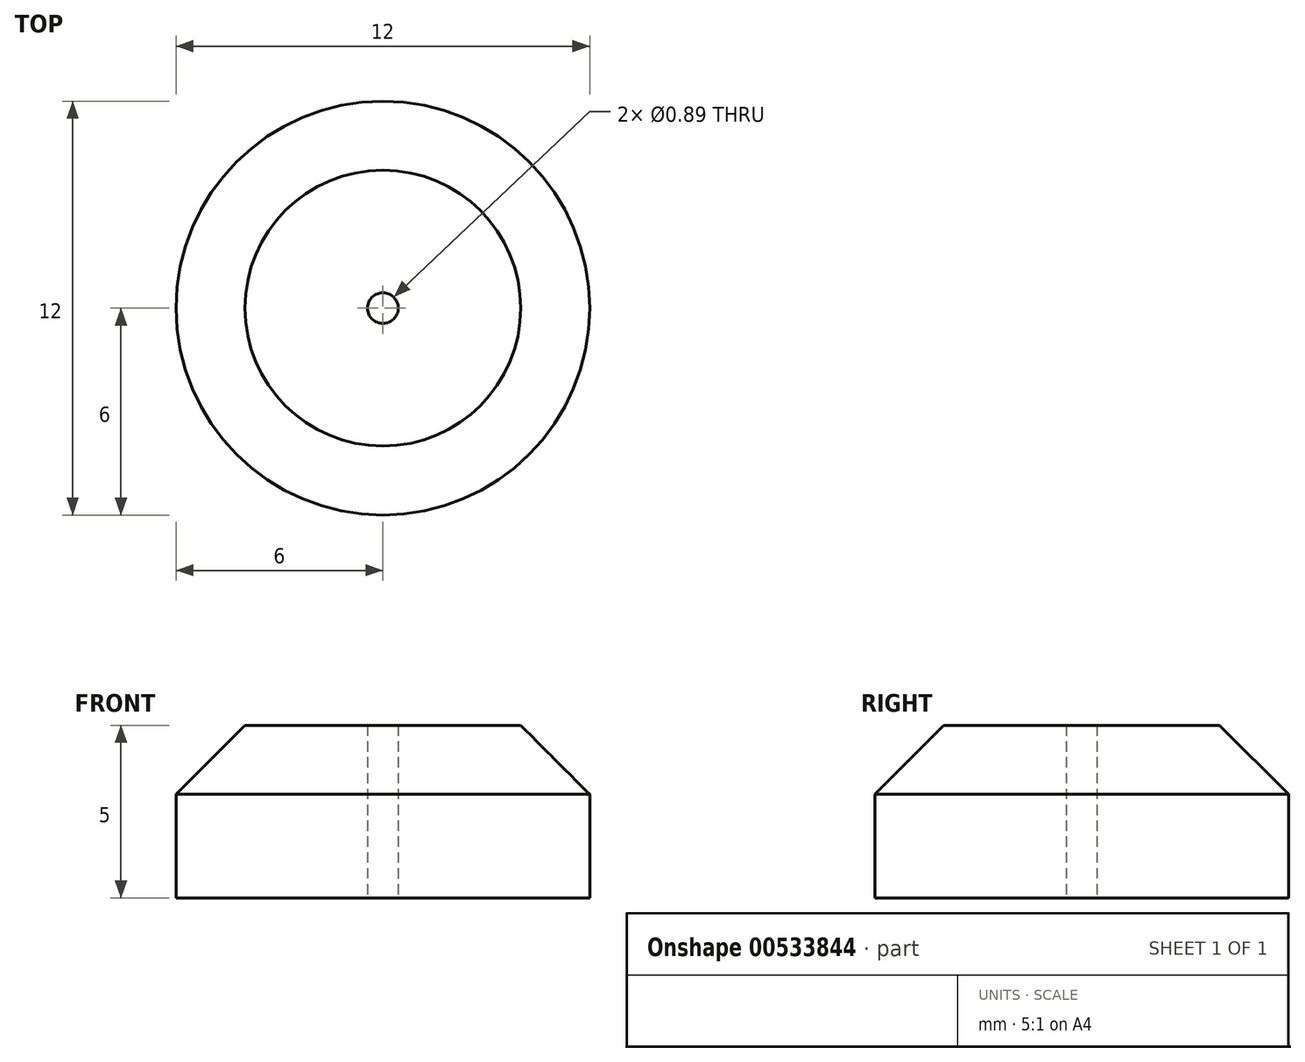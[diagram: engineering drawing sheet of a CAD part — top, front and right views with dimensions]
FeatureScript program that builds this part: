
annotation { "Feature Type Name" : "Feature", "Feature Type Description" : "" }
export const myFeature = defineFeature(function(context is Context, id is Id, definition is map)
    precondition{}
    {
        {
            var Q0;
            Q0=qCreatedBy(makeId("Top.planeOp"),FACE);
            var sketch = newSketch(context, id + "F0", { "sketchPlane" : qUnion([Q0])});
            skCircle(sketch, "E0", {"center": v(0, 0) * mm, "radius": 6 * mm});
            skCircle(sketch, "E1", {"center": v(0, 0) * mm, "radius": 0.45 * mm});
            skCircle(sketch, "E2", {"center": v(0, 0) * mm, "radius": 5 * mm});
            skSolve(sketch);
        }
        {
            var Q0;
            Q0=makeQuery(id+"F0.imprint","IMPRINT",FACE,{"disambiguationData":[TD([[makeQuery(id+"F0.imprint","IMPRINT",EDGE,{"derivedFrom":sQuery(id+"F0.wireOp",EDGE,"E1")}),-1.0]])]});
            var Q1;
            Q1=makeQuery(id+"F0.imprint","IMPRINT",FACE,{"disambiguationData":[TD([[makeQuery(id+"F0.imprint","IMPRINT",EDGE,{"derivedFrom":sQuery(id+"F0.wireOp",EDGE,"E0")}),1.0]])]});
            extrude(context, id + "F1", {"entities" : qUnion([Q0, Q1]), "depth" : 5 * mm, "offsetDistance" : 25.4 * mm});
        }
        {
            var Q0;
            Q0=makeQuery(id+"F1.opExtrude","CAP_EDGE",EDGE,{"disambiguationData":[OSD([sQuery(id+"F0.wireOp",EDGE,"E0")])],"isStart":false});
            chamfer(context, id + "F2", {"entities" : qUnion([Q0]), "width" : 2 * mm, "tangentPropagation" : true});
        }
    });
